# Revit family: leddownlightmw-p2_rd200-22w-ble2-930_940_540001386100_33f5
name_source: partatom
category: Lighting Fixtures
units: mm (PartAtom-declared; Revit-internal decimal feet)

## family parameters
Cut with Voids When Loaded = No
Host = Face
Light Source = No
Part Type = Normal
Room Calculation Point = No
Round Connector Dimension = Use Diameter
Shared = No

## types (1)
- LEDDownlightMW-P2 Rd200-22W-BLE2-930/940 (1 x LED, 2860 lm, 4000)
    Apparent Load = 22 VA
    Approval mark = CE, ENEC
    CIE Flux Codes = 75 96 100 100 100
    Color Rendering = 90
    Color Temperature = 4000
    Control Gear = Electronic ballast
    Default Elevation = 1800 mm
    Description = Downlight Performer G2 MW Ø226mm-22W-2640lm-3/4000K-CRI90
    Frequency = 60 Hz
    Height = 0 mm  [stored 0 ft]
    Lamp = 1 x LED
    Lamp Light Flux = 2860 lm
    Lamp count = 1
    Length = 226 mm
    Luminous efficacy = 130 lm/W
    Manufacturer = OPPLE
    ModVariant = No
    Model = 540001386100
    Mounting Place = Floor
    Mounting Type = Recessed
    Number of Poles = 1
    OnlyDefault = Yes
    Power Factor = 1
    Product Name = LEDDownlightMW-P2 Rd200-22W-BLE2-930/940
    ProductGroupID = 3327
    Protection Class = Protection class II
    Protection Degree = IP 54
    RLX_Detail_Level = 1
    RLX_Emergency_Light_Flux = 0 lm
    RLX_Emergency_Type = 0
    RLX_Emergency_Type_DB = No
    RlxData = <blob elided: 303453 chars, md5=e57ce627>
    Socket = socket
    Standby Power = 0 W
    System Light Flux = 2860 lm
    System Power = 22 W
    Type Comments = Product without accessories
    Type Image = web_downmw_p2_r200.jpg
    URL = http://relux.com
    VarID = ---
    Voltage = 230 V
    Voltage Range = 220-240 V
    Weight = 0.00 kg
    Width = 226 mm

note: [stored X ft] marks values corroborated as IEEE doubles in the binary element streams (Revit-internal decimal feet)

## geometry (parser evidence)
native form markers: Blend x4, Sweep x10
no freeform markers — native parametric forms only
